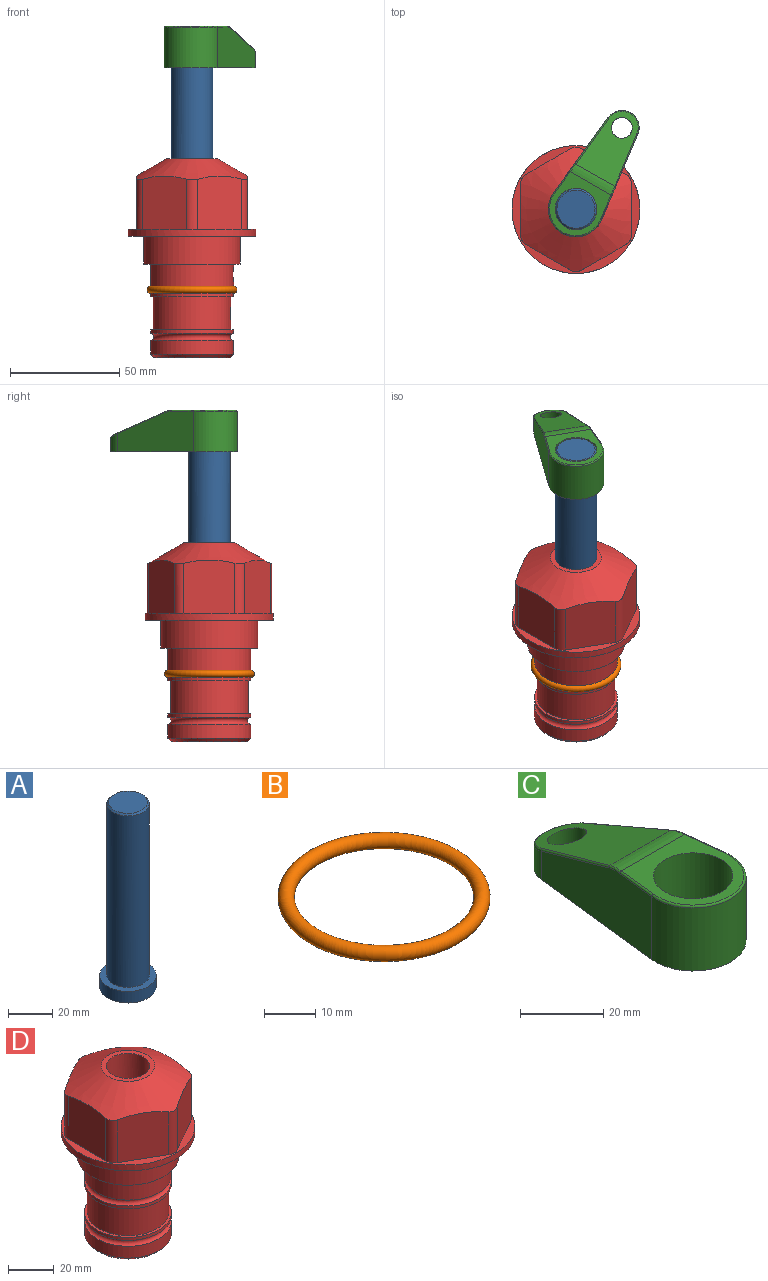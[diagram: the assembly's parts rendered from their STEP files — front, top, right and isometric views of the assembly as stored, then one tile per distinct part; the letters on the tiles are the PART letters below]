
ASSEMBLY  parts=4 mates=2
PART A: 6 faces, bbox 25.4x25.4x101.6 mm
  f0: plane 17.46x17.46mm, normal (0,0,1), area 239.5mm2, adj f5
  f1: plane 25.4x25.4mm, normal (0,0,-1), area 506.7mm2, adj f2
  f2: cylinder r=12.7mm len=25.4mm, axis (0,0,1), area 506.7mm2, adj f1,f3
  f3: plane 25.4x25.4mm, normal (0,0,1), area 221.7mm2, adj f2,f4
  f4: cylinder r=9.53mm len=94.46mm, axis (0,0,1), area 5653mm2, adj f3,f5
  f5: cone r=8.73mm half-angle=45deg, axis (0,0,-1), area 64.4mm2, adj f0,f4
PART B: 1 faces, bbox 44.7x44.7x3.2 mm
  f0: torus R=19.05mm, axis (0,0,1), area 1193.9mm2
PART C: 44 faces, bbox 27.5x64.5x19.1 mm
  f0: plane 2.3x0.95mm, normal (0,0,-1), area 1mm2, adj f25,f30,f34
  f1: plane 63.5x25.4mm, normal (0,0,-1), area 561.7mm2, adj f2,f3,f4,f5,f6,f7,f19,f20
  f2: cylinder r=12.7mm len=25.4mm, axis (0,0,-1), area 792.2mm2, adj f1,f3,f5,f13
  f3: plane 42.33x18.54mm, normal (0.99,0.11,0), area 647mm2, adj f1,f2,f4,f11,f12,f14
  f4: cylinder r=7.94mm len=15.78mm, axis (0,0,-1), area 158.6mm2, adj f1,f3,f5,f16
  f5: plane 42.33x18.54mm, normal (-0.99,0.11,0), area 647mm2, adj f1,f2,f4,f15,f17,f18
  f6: cylinder r=9.53mm len=19.05mm, axis (0,0,-1), area 1140.1mm2, adj f1,f8
  f7: cylinder r=4.76mm len=10.98mm, axis (0,0,-1), area 276.1mm2, adj f1,f9
  f8: plane 25.83x24.38mm, normal (0,0,1), area 262.2mm2, adj f6,f10,f11,f13,f15
  f9: plane 32.49x20.55mm, normal (0,0.34,0.94), area 489.9mm2, adj f7,f10,f14,f16,f18
  f10: cylinder r=12.7mm len=21.49mm, axis (-1,0,0), area 93.2mm2, adj f8,f9,f12,f17
  f11: cylinder r=0.51mm len=12.34mm, axis (0.11,-0.99,0), area 9.9mm2, adj f3,f8,f12,f13
  f12: bspline ~7.62x1.64mm, area 3.5mm2, adj f3,f10,f11,f14
  f13: torus R=12.19mm, axis (0,0,1), area 33.6mm2, adj f2,f8,f11,f15
  f14: cylinder r=0.51mm len=26.01mm, axis (0.1,-0.93,0.34), area 21.6mm2, adj f3,f9,f12,f16
  f15: cylinder r=0.51mm len=12.34mm, axis (0.11,0.99,0), area 9.9mm2, adj f5,f8,f13,f17
  f16: bspline ~15.78x7.05mm, area 15.7mm2, adj f4,f9,f14,f18
  f17: bspline ~7.62x1.64mm, area 3.5mm2, adj f5,f10,f15,f18
  f18: cylinder r=0.51mm len=26.01mm, axis (0.1,0.93,-0.34), area 21.6mm2, adj f5,f9,f16,f17
  f19: plane 21.6x14.29mm, normal (-0.99,-0.11,0), area 242.6mm2, adj f1,f26,f28,f34,f36,f38
  f20: plane 21.6x14.29mm, normal (0.99,-0.11,0), area 242.6mm2, adj f1,f27,f29,f37,f39,f41
  f21: cylinder r=12.7mm len=14.29mm, axis (0,0,-1), area 173.2mm2, adj f1,f26,f27,f30,f31,f33
  f22: cylinder r=7.94mm len=7.63mm, axis (0,0,-1), area 53.8mm2, adj f1,f28,f29,f42
  f23: plane 2.3x0.95mm, normal (0,0,-1), area 1mm2, adj f25,f33,f37
  f24: plane 17.94x12.32mm, normal (0,-0.34,-0.94), area 191.2mm2, adj f25,f38,f41,f42
  f25: cylinder r=9.53mm len=12.93mm, axis (-1,0,0), area 37.5mm2, adj f0,f23,f24,f31,f36,f39
  f26: cylinder r=1.59mm len=14.29mm, axis (0,0,-1), area 49mm2, adj f1,f19,f21,f32
  f27: cylinder r=1.59mm len=14.29mm, axis (0,0,-1), area 49mm2, adj f1,f20,f21,f35
  f28: cylinder r=1.59mm len=7.28mm, axis (0,0,-1), area 22.1mm2, adj f1,f19,f22,f40
  f29: cylinder r=1.59mm len=7.28mm, axis (0,0,-1), area 22.1mm2, adj f1,f20,f22,f43
  f30: torus R=14.29mm, axis (0,0,1), area 5.8mm2, adj f0,f21,f31,f32
  f31: bspline ~11.06x2.73mm, area 20.8mm2, adj f21,f25,f30,f33
  f32: sphere r=1.59mm, area 5.4mm2, adj f26,f30,f34
  f33: torus R=14.29mm, axis (0,0,1), area 5.8mm2, adj f21,f23,f31,f35
  f34: cylinder r=1.59mm len=1.68mm, axis (-0.11,0.99,0), area 2.4mm2, adj f0,f19,f32,f36
  f35: sphere r=1.59mm, area 5.4mm2, adj f27,f33,f37
  f36: bspline ~5.82x2.33mm, area 7.7mm2, adj f19,f25,f34,f38
  f37: cylinder r=1.59mm len=1.68mm, axis (0.11,0.99,0), area 2.4mm2, adj f20,f23,f35,f39
  f38: cylinder r=1.59mm len=18.33mm, axis (0.1,-0.93,0.34), area 46.7mm2, adj f19,f24,f36,f40
  f39: bspline ~5.82x2.33mm, area 7.7mm2, adj f20,f25,f37,f41
  f40: sphere r=1.59mm, area 3.6mm2, adj f28,f38,f42
  f41: cylinder r=1.59mm len=18.33mm, axis (0.1,0.93,-0.34), area 46.7mm2, adj f20,f24,f39,f43
  f42: bspline ~8.31x1.84mm, area 15.3mm2, adj f22,f24,f40,f43
  f43: sphere r=1.59mm, area 3.6mm2, adj f29,f41,f42
PART D: 36 faces, bbox 58.7x58.7x91.2 mm
  f0: cylinder r=17.78mm len=35.56mm, axis (0,0,1), area 1670.8mm2, adj f23,f24,f31
  f1: cylinder r=19.05mm len=38.1mm, axis (0,0,1), area 1191.9mm2, adj f26,f27,f30
  f2: plane 58.66x58.66mm, normal (0,0,-1), area 1150.6mm2, adj f3,f28
  f3: cylinder r=29.33mm len=58.66mm, axis (0,0,-1), area 585.1mm2, adj f2,f4
  f4: plane 58.66x58.66mm, normal (0,0,1), area 475.9mm2, adj f3,f5,f6,f7,f8,f9,f10,f11
  f5: plane 24.5x20.32mm, normal (-0.5,0.87,0), area 562.8mm2, adj f4,f15,f16,f17
  f6: plane 24.5x20.32mm, normal (0.5,0.87,0), area 562.8mm2, adj f4,f14,f15,f17
  f7: plane 24.5x23.48mm, normal (1,0,0), area 562.8mm2, adj f4,f13,f14,f17
  f8: plane 24.5x20.32mm, normal (0.5,-0.87,0), area 562.8mm2, adj f4,f12,f13,f17
  f9: plane 24.5x20.32mm, normal (-0.5,-0.87,0), area 562.8mm2, adj f4,f11,f12,f17
  f10: plane 24.5x23.48mm, normal (-1,0,0), area 562.8mm2, adj f4,f11,f16,f17
  f11: cylinder r=5.08mm len=23.01mm, axis (0,0,-1), area 121.2mm2, adj f4,f9,f10,f17
  f12: cylinder r=5.08mm len=23.01mm, axis (0,0,-1), area 121.2mm2, adj f4,f8,f9,f17
  f13: cylinder r=5.08mm len=23.01mm, axis (0,0,-1), area 121.2mm2, adj f4,f7,f8,f17
  f14: cylinder r=5.08mm len=23.01mm, axis (0,0,-1), area 121.2mm2, adj f4,f6,f7,f17
  f15: cylinder r=5.08mm len=23.01mm, axis (0,0,-1), area 121.2mm2, adj f4,f5,f6,f17
  f16: cylinder r=5.08mm len=23.01mm, axis (0,0,-1), area 121.2mm2, adj f4,f5,f10,f17
  f17: cone r=11.73mm half-angle=60deg, axis (0,0,-1), area 2071.8mm2, adj f5,f6,f7,f8,f9,f10,f11,f12
  f18: plane 23.46x23.46mm, normal (0,0,1), area 147.4mm2, adj f17,f35
  f19: plane 34.93x34.93mm, normal (0,0,-1), area 958mm2, adj f29
  f20: cylinder r=19.05mm len=38.1mm, axis (0,0,1), area 760.1mm2, adj f21,f29
  f21: torus R=19.05mm, axis (0,0,1), area 565.3mm2, adj f20,f22
  f22: cylinder r=19.05mm len=38.1mm, axis (0,0,1), area 190mm2, adj f21,f23
  f23: plane 38.1x38.1mm, normal (0,0,1), area 146.9mm2, adj f0,f22
  f24: plane 38.1x38.1mm, normal (0,0,-1), area 146.9mm2, adj f0,f25
  f25: cylinder r=19.05mm len=38.1mm, axis (0,0,1), area 190mm2, adj f24,f26
  f26: torus R=19.05mm, axis (0,0,1), area 565.3mm2, adj f1,f25
  f27: plane 44.45x44.45mm, normal (0,0,-1), area 411.7mm2, adj f1,f28
  f28: cylinder r=22.23mm len=44.45mm, axis (0,0,1), area 1773.5mm2, adj f2,f27
  f29: cone r=19.05mm half-angle=45deg, axis (0,0,1), area 257.5mm2, adj f19,f20
  f30: cylinder r=3.17mm len=6.75mm, axis (-1,0,0), area 128mm2, adj f1,f33
  f31: cylinder r=3.17mm len=6.35mm, axis (-1,0,0), area 102.5mm2, adj f0,f33
  f32: plane 25.4x25.4mm, normal (0,0,1), area 506.7mm2, adj f33
  f33: cylinder r=12.7mm len=66.42mm, axis (0,0,-1), area 5236.2mm2, adj f30,f31,f32,f34
  f34: cone r=9.53mm half-angle=30deg, axis (0,0,-1), area 443.4mm2, adj f33,f35
  f35: cylinder r=9.53mm len=19.05mm, axis (0,0,-1), area 849mm2, adj f18,f34
PLACE A rot(axis=(0,0,-1),29.4deg) t=(0,0,22.65)mm
PLACE B at identity
PLACE C rot(axis=(0,0,-1),29.4deg) t=(0,0,77.26)mm
PLACE D at identity fixed
MATE fastened C.f2 <-> A.f2  axis (0,0,-1) through (0,0,96.31)mm
MATE cylindrical A.f2 <-> D.f0  axis (0,0,1) through (0,0,48.29)mm
